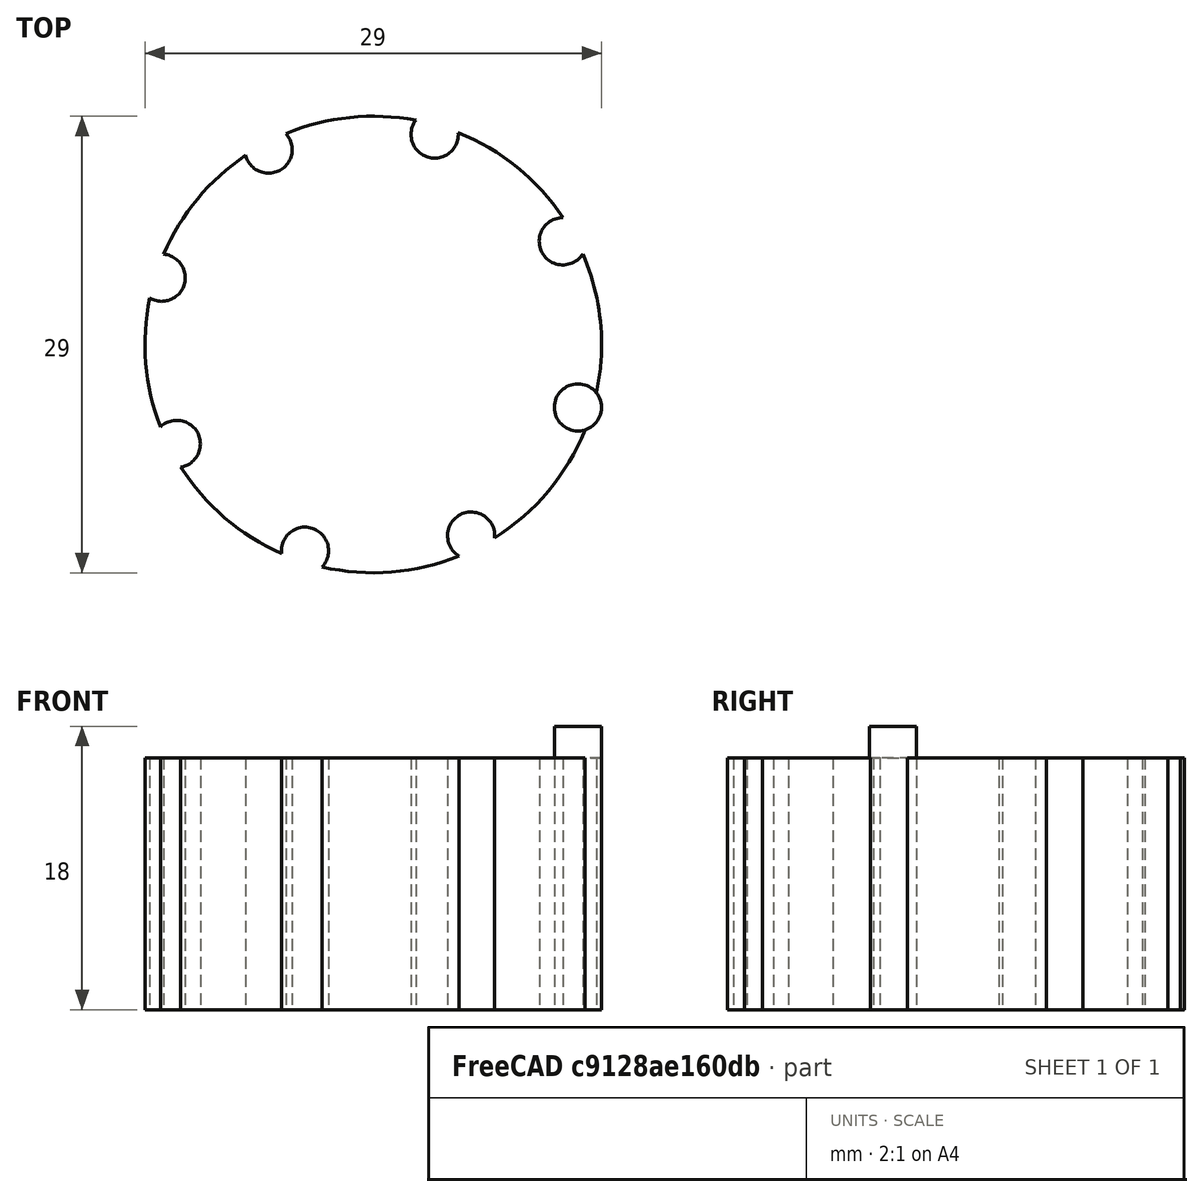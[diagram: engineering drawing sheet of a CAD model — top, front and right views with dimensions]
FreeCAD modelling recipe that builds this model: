
FCSTD DOCUMENT  (FreeCAD 1.0R39319 (Git))
Label: ojt1_t11r01_buttom1
License: All rights reserved
LicenseURL: https://en.wikipedia.org/wiki/All_rights_reserved
objects: Part::Cylinder×2, Part::FeaturePython×1, Part::Cut×1
note: 3 computed .brp shape members not serialized (recipe doc carries the construction recipe); baked Part::Feature solids carry a one-line shape summary decoded from their .brp

FEATURE [Part::Cylinder] Cylinder  label="Cilindre"
  Angle = 360
  AttacherType = Attacher::AttachEngine3D
  FirstAngle = 0
  Height = 18
  Radius = 1.5
  SecondAngle = 0
FEATURE [Part::FeaturePython] Array  # Draft array (typed FeaturePython)
  AlwaysSyncPlacement = false
  Angle = 360
  ArrayType = 1
  Axis = (0,0,1)
  Base = -> Cylinder
  Center = (-13.22,4.12,0)
  Count = 8
  ExpandArray = false
  Fuse = false
  IntervalAxis = (0,0,0)
  IntervalX = (50,0,0)
  IntervalY = (0,50,0)
  IntervalZ = (0,0,50)
  NumberCircles = 3
  NumberPolar = 8
  NumberX = 2
  NumberY = 2
  NumberZ = 1
  PlacementList = 8 placements: [(0,0,0),(-0.958768,10.5547,0),(-9.1,17.34,0),(-19.6547,16.3812,0),(-26.44,8.24,0),(-25.4812,-2.31467,0),(-17.34,-9.1,0),(-6.78533,-8.14123,0)]
  RadialDistance = 50
  ScaleList = (8) [(1,1,1),(1,1,1),(1,1,1),(1,1,1),(1,1,1),(1,1,1),(1,1,1),(1,1,1)]
  Symmetry = 1
  TangentialDistance = 25
FEATURE [Part::Cylinder] Cylinder001  label="Cilindre001"
  Angle = 360
  AttacherType = Attacher::AttachEngine3D
  FirstAngle = 0
  Height = 16
  Placement = pos=(-13,4,0) rot=(0,0,1;0rad)
  Radius = 14.5
  SecondAngle = 0
FEATURE [Part::Cut] Cut
  Base = -> Cylinder001
  Refine = true
  Tool = -> Array
